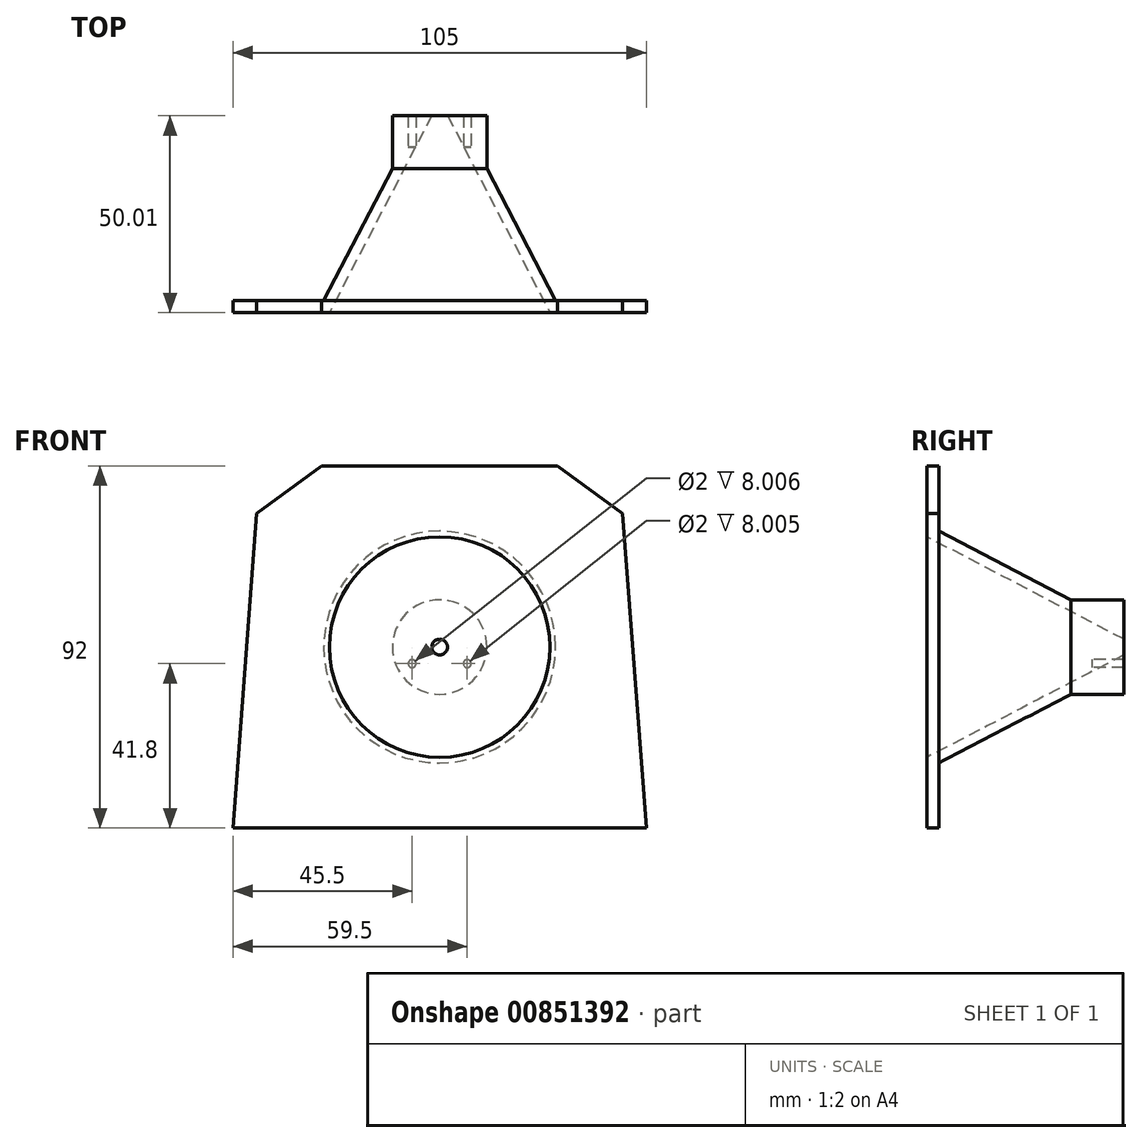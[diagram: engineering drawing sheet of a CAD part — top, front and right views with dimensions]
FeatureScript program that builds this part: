
annotation { "Feature Type Name" : "Feature", "Feature Type Description" : "" }
export const myFeature = defineFeature(function(context is Context, id is Id, definition is map)
    precondition{}
    {
        {
            var Q0;
            Q0=qCreatedBy(makeId("Front.planeOp"),FACE);
            var sketch = newSketch(context, id + "F0", { "sketchPlane" : qUnion([Q0])});
            skLineSegment(sketch, "E0", {"start": v(52.5, -46) * mm, "end": v(-52.5, -46) * mm});
            skLineSegment(sketch, "E1", {"start": v(-46.5, 34) * mm, "end": v(-52.5, -46) * mm});
            skLineSegment(sketch, "E2", {"start": v(46.5, 34) * mm, "end": v(52.5, -46) * mm});
            skLineSegment(sketch, "E3", {"start": v(-30, 46) * mm, "end": v(30, 46) * mm});
            skLineSegment(sketch, "E4", {"start": v(-46.5, 34) * mm, "end": v(-30, 46) * mm});
            skLineSegment(sketch, "E5", {"start": v(30, 46) * mm, "end": v(46.5, 34) * mm});
            skLineSegment(sketch, "E6", {"start": v(0, 0) * mm, "end": v(0, -4.2) * mm});
            skLineSegment(sketch, "E7", {"start": v(0, -4.2) * mm, "end": v(7, -4.2) * mm});
            skLineSegment(sketch, "E8", {"start": v(0, -4.2) * mm, "end": v(-7, -4.2) * mm});
            skCircle(sketch, "E9", {"center": v(-7, -4.2) * mm, "radius": 1 * mm});
            skCircle(sketch, "E10", {"center": v(7, -4.2) * mm, "radius": 1 * mm});
            skSolve(sketch);
        }
        {
            var Q0;
            Q0=makeQuery(id+"F0.imprint","IMPRINT",FACE,{"disambiguationData":[TD([[makeQuery(id+"F0.imprint","IMPRINT",EDGE,{"derivedFrom":sQuery(id+"F0.wireOp",EDGE,"E0")}),-1.0]])]});
            extrude(context, id + "F1", {"entities" : qUnion([Q0]), "oppositeDirection" : true, "depth" : 3 * mm, "offsetDistance" : 25 * mm});
        }
        {
            var Q0;
            Q0=qCreatedBy(makeId("Top.planeOp"),FACE);
            var sketch = newSketch(context, id + "F2", { "sketchPlane" : qUnion([Q0])});
            skLineSegment(sketch, "E11", {"start": v(0, 0) * mm, "end": v(-20, 0) * mm});
            skLineSegment(sketch, "E12", {"start": v(-20, 0) * mm, "end": v(-22, 0) * mm});
            skLineSegment(sketch, "E13", {"start": v(0, 0) * mm, "end": v(-28, 0) * mm});
            skLineSegment(sketch, "E14", {"start": v(0, 0) * mm, "end": v(0, 50) * mm});
            skLineSegment(sketch, "E15", {"start": v(-28, 0) * mm, "end": v(-31, 0) * mm});
            skLineSegment(sketch, "E16", {"start": v(0, 0) * mm, "end": v(-2, 0) * mm});
            skLineSegment(sketch, "E17", {"start": v(0, 50) * mm, "end": v(-12, 50) * mm});
            skLineSegment(sketch, "E18", {"start": v(0, 50) * mm, "end": v(-2, 50) * mm});
            skLineSegment(sketch, "E19", {"start": v(-2, 50) * mm, "end": v(-2, 0) * mm});
            skLineSegment(sketch, "E20", {"start": v(-2, 50) * mm, "end": v(-28, 0) * mm});
            skLineSegment(sketch, "E21", {"start": v(-2, 50) * mm, "end": v(-5, 50) * mm});
            skLineSegment(sketch, "E22", {"start": v(-5, 50) * mm, "end": v(-31, 0) * mm});
            skLineSegment(sketch, "E23", {"start": v(-12, 50) * mm, "end": v(-12, 36.54) * mm});
            skSolve(sketch);
        }
        {
            var Q0;
            {var subQ3=sQuery(id+"F2.wireOp",EDGE,"E15");Q0=makeQuery(id+"F2.imprint","IMPRINT",FACE,{"disambiguationData":[TD([[makeQuery(id+"F2.imprint","IMPRINT",EDGE,{"derivedFrom":subQ3}),-1.0]])]});}
            var Q1;
            {var subQ0=sQuery(id+"F2.wireOp",EDGE,"E17");Q1=makeQuery(id+"F2.imprint","IMPRINT",FACE,{"disambiguationData":[TD([[makeQuery(id+"F2.imprint","IMPRINT",EDGE,{"derivedFrom":subQ0}),1.0]])]});}
            var Q2;
            Q2=sQuery(id+"F2.wireOp",EDGE,"E14");
            revolve(context, id + "F3", {"operationType" : NewBodyOperationType.ADD, "surfaceOperationType" : NewSurfaceOperationType.NEW, "entities" : qUnion([Q0, Q1]), "axis" : qUnion([Q2]), "revolveType" : RevolveType.FULL});
        }
        {
            var Q0;
            {var subQ0=sQuery(id+"F2.wireOp",EDGE,"E19");Q0=makeQuery(id+"F2.imprint","IMPRINT",FACE,{"disambiguationData":[TD([[makeQuery(id+"F2.imprint","IMPRINT",EDGE,{"derivedFrom":subQ0}),-1.0]])]});}
            var Q1;
            Q1=makeQuery(id+"F2.imprint","IMPRINT",FACE,{"disambiguationData":[TD([[makeQuery(id+"F2.imprint","IMPRINT",EDGE,{"derivedFrom":sQuery(id+"F2.wireOp",EDGE,"E14")}),1.0]])]});
            var Q2;
            Q2=makeQuery(id+"F3.opRevolve","SWEPT_EDGE",EDGE,{"disambiguationData":[OSD([sQuery(id+"F2.wireOp",EDGE,"E18"),sQuery(id+"F2.wireOp",EDGE,"E19"),sQuery(id+"F2.wireOp",EDGE,"E20"),sQuery(id+"F2.wireOp",EDGE,"E21")])]});
            revolve(context, id + "F4", {"operationType" : NewBodyOperationType.REMOVE, "surfaceOperationType" : NewSurfaceOperationType.NEW, "entities" : qUnion([Q0, Q1]), "axis" : qUnion([Q2]), "revolveType" : RevolveType.FULL, "oppositeDirection" : true});
        }
        {
            var Q0;
            Q0=makeQuery(id+"F0.imprint","IMPRINT",FACE,{"disambiguationData":[TD([[makeQuery(id+"F0.imprint","IMPRINT",EDGE,{"derivedFrom":sQuery(id+"F0.wireOp",EDGE,"E10")}),1.0]])]});
            var Q1;
            Q1=makeQuery(id+"F0.imprint","IMPRINT",FACE,{"disambiguationData":[TD([[makeQuery(id+"F0.imprint","IMPRINT",EDGE,{"derivedFrom":sQuery(id+"F0.wireOp",EDGE,"E9")}),1.0]])]});
            extrude(context, id + "F5", {"entities" : qUnion([Q0, Q1]), "operationType" : NewBodyOperationType.REMOVE, "oppositeDirection" : true, "depth" : 51 * mm, "offsetDistance" : 25 * mm, "hasSecondDirection" : true, "secondDirectionOppositeDirection" : true, "secondDirectionDepth" : 42 * mm});
        }
    });
